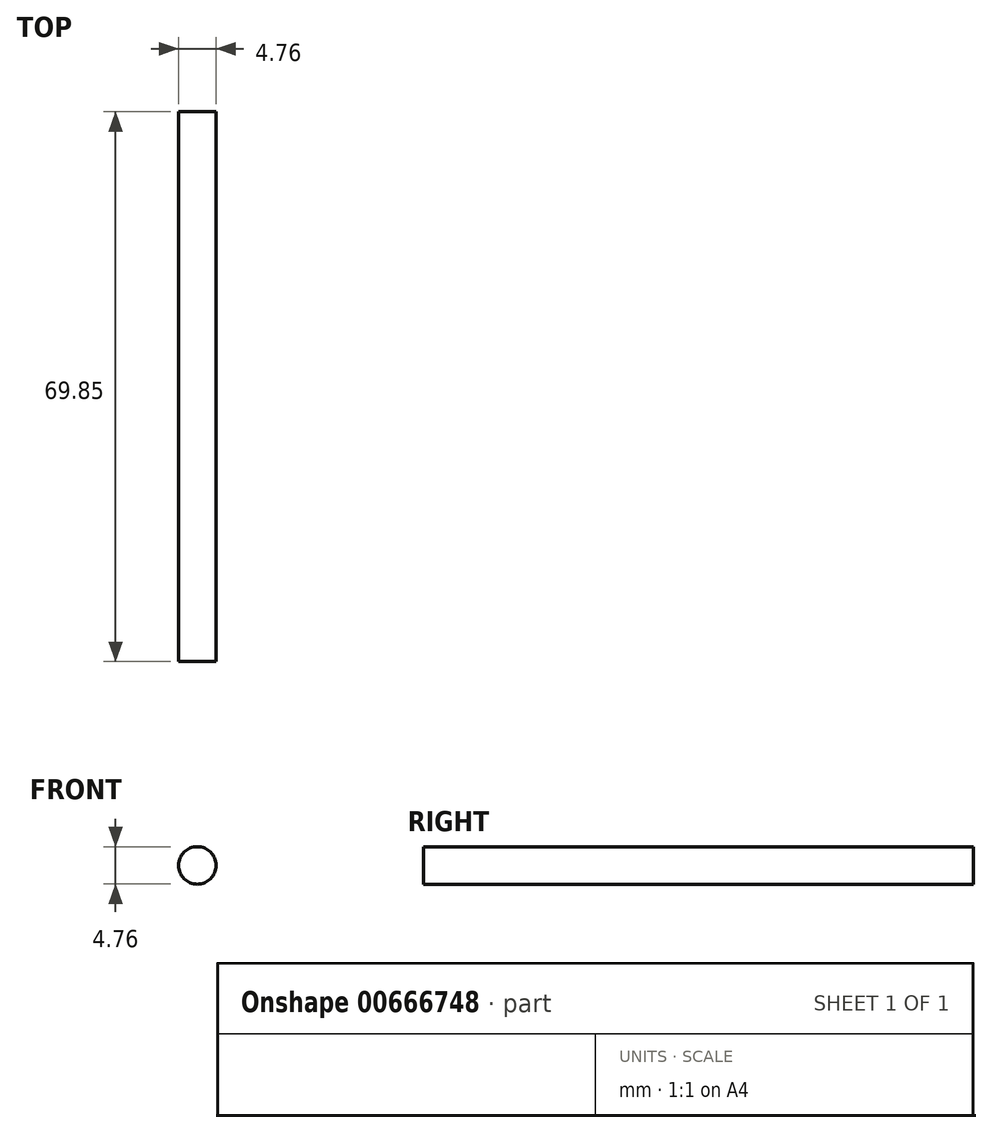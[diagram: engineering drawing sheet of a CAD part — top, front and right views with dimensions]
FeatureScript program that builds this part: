
annotation { "Feature Type Name" : "Feature", "Feature Type Description" : "" }
export const myFeature = defineFeature(function(context is Context, id is Id, definition is map)
    precondition{}
    {
        {
            var Q0;
            Q0=qCreatedBy(makeId("Front.planeOp"),FACE);
            var sketch = newSketch(context, id + "F0", { "sketchPlane" : qUnion([Q0])});
            skCircle(sketch, "E0", {"center": v(0, 0) * mm, "radius": 2.38 * mm});
            skSolve(sketch);
        }
        {
            var Q0;
            Q0 = qSketchRegion(id + "F0", true);
            extrude(context, id + "F1", {"entities" : qUnion([Q0]), "depth" : 69.85 * mm, "offsetDistance" : 25.4 * mm});
        }
    });
